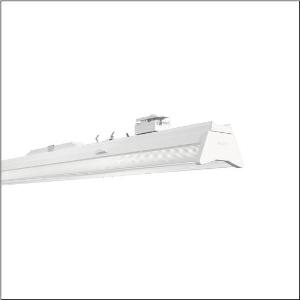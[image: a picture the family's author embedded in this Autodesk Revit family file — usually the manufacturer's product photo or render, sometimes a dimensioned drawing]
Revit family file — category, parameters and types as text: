
# Revit family: licross_r__11_performance_mo_51tm16dn35xg_3127
name_source: partatom
category: Lighting Fixtures
units: mm (PartAtom-declared; Revit-internal decimal feet)

## family parameters
Cut with Voids When Loaded = No
Host = Face
Light Source = No
Part Type = Normal
Room Calculation Point = No
Round Connector Dimension = Use Diameter
Shared = No

## types (1)
- --- (1 x LED, 5100 lm, 28.3 W, 3000K)
    Apparent Load = 28 VA
    CIE Flux Codes = 66 88 96 79 100
    Color Rendering = 80
    Color Temperature = 3000K
    Default Elevation = 1800 mm
    Description = Licross® 11 Performance MO, luminaire insert, of sheet steel, galvanised, coil coated, white, length: 1.500mm, width: 120mm, height: 123mm, LED rated luminous flux: 5.100lm, light colour: 830, control gear: DALI 2, with plug, 5-pole, with phase selection, mains connection: 220..240V, AC, 50/60Hz, rated input power: 28.3W, halogen-free wiring, primary light control with lens, of plastic, primary optical cover: cover, of PMMA, light emission: direct/indirect distribution, primary light characteristic: symmetric, protection rating (complete): IP40, insulation class (complete): insulation class I (protective earthing), certification: CE, ENEC, VDE, UKCA, protection symbol: D if used in an environment without relevant dust loads with corresponding accessories, impact resistance: IK06, permissible ambient temperature for indoor applications: -25..+45°C, corresponds to IFS (International Featured Standards) requirements for safety and quality in the food industry, reducing of maximum allowable ambient temperature of 5°C with ceiling mounting, LABS conformity tested according to VDMA 24364:2018-05, packaging unit: 1 piece
    Height = 114 mm
    Lamp = 1 x LED
    Lamp Light Flux = 5100 lm
    Lamp Power = 28.3 W
    Lamp count = 1
    Length = 1500 mm
    Luminous efficacy = 180 lm/W
    Manufacturer = Siteco
    ModVariant = No
    Model = 51TM16DN35XG
    Mounting Place = Ceiling
    Mounting Type = Pendant
    Number of Poles = 1
    OnlyDefault = Yes
    Power Factor = 1
    Product Name = Licross® 11 Performance MO
    Product group = luminaire insert
    ProductGroupID = 901
    Protection Class = Protection class I
    Protection Degree = IP 40
    RLX_Detail_Level = 1
    RLX_Emergency_Light_Flux = 0 lm
    RLX_Emergency_Type = 0
    RLX_Emergency_Type_DB = No
    RlxData = <blob elided: 33877 chars, md5=0d37c8a5>
    Socket = socket
    Standby Power = 0 W
    System Light Flux = 5100 lm
    System Power = 28 W
    Type Comments = factory setting: luminous flux: 100 % | dim-lin: 254 | 190 mA
    Type Image = l_1256138.jpg
    URL = http://relux.com
    VarID = @adj_036233
    Voltage = 0 V
    Weight = 0.00 kg
    Width = 120 mm

## geometry (parser evidence)
native form markers: Blend x4, Sweep x10
no freeform markers — native parametric forms only
